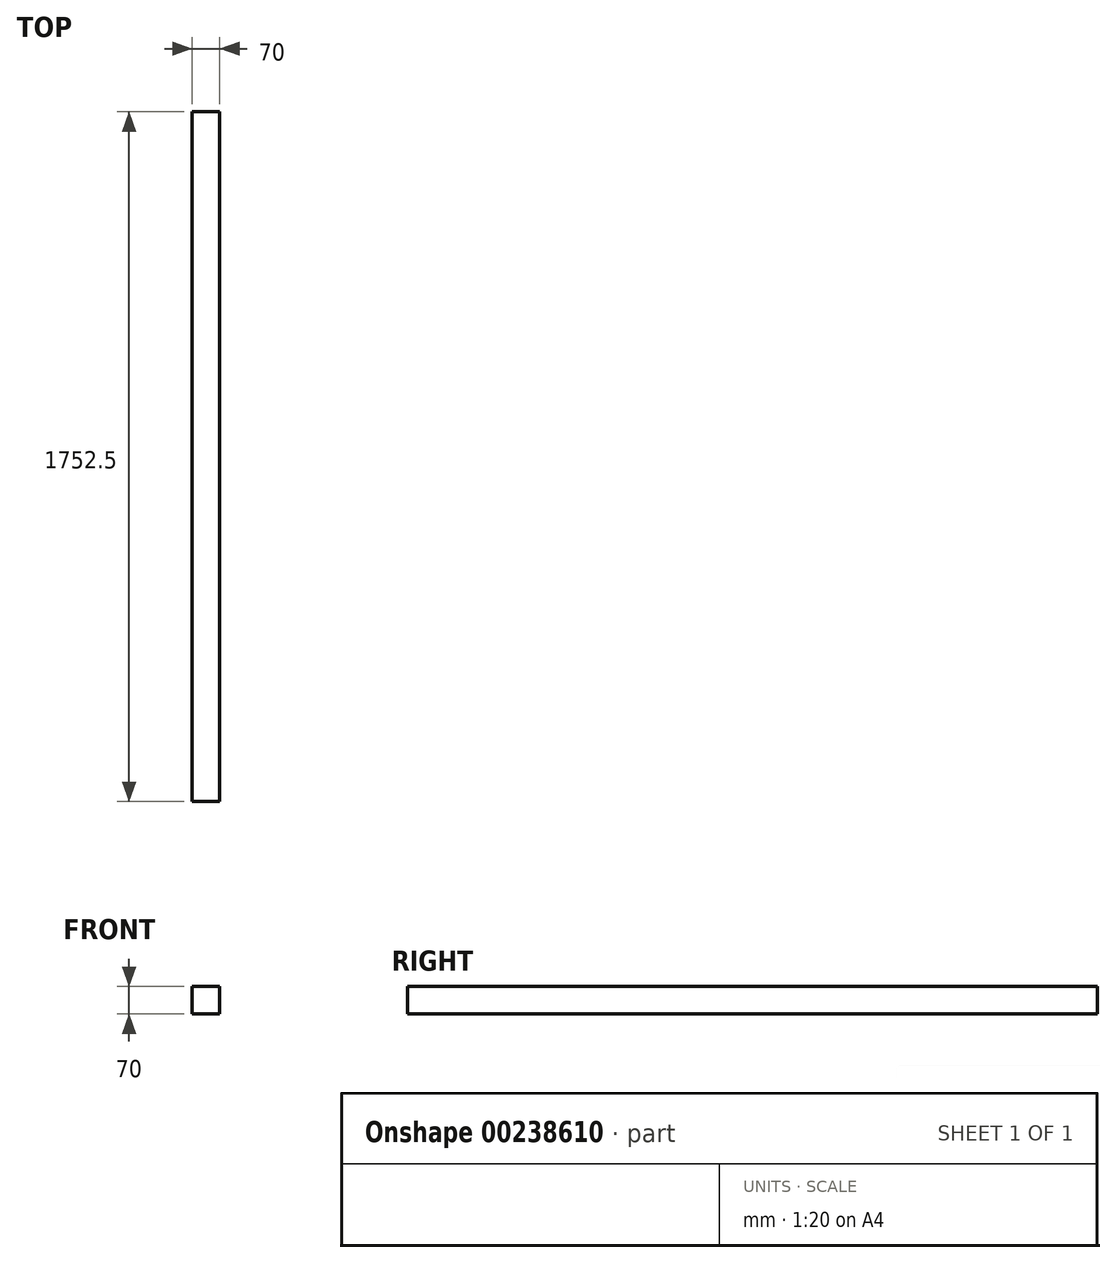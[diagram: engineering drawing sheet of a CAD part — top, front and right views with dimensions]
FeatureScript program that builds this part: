
annotation { "Feature Type Name" : "Feature", "Feature Type Description" : "" }
export const myFeature = defineFeature(function(context is Context, id is Id, definition is map)
    precondition{}
    {
        {
            var Q0;
            Q0=qCreatedBy(makeId("Front.planeOp"),FACE);
            var sketch = newSketch(context, id + "F0", { "sketchPlane" : qUnion([Q0])});
            skLineSegment(sketch, "E0.bottom", {"start": v(35, -35) * mm, "end": v(-35, -35) * mm});
            skLineSegment(sketch, "E0.top", {"start": v(35, 35) * mm, "end": v(-35, 35) * mm});
            skLineSegment(sketch, "E0.left", {"start": v(35, -35) * mm, "end": v(35, 35) * mm});
            skLineSegment(sketch, "E0.right", {"start": v(-35, -35) * mm, "end": v(-35, 35) * mm});
            skPoint(sketch, "E0.middle", {"position": v(0, 0) * mm});
            skSolve(sketch);
        }
        {
            var Q0;
            Q0=makeQuery(id+"F0.imprint","IMPRINT",FACE,{"disambiguationData":[TD([[makeQuery(id+"F0.imprint","IMPRINT",EDGE,{"derivedFrom":sQuery(id+"F0.wireOp",EDGE,"E0.bottom")}),-1.0]])]});
            extrude(context, id + "F1", {"entities" : qUnion([Q0]), "depth" : (1302.5 + 450) * mm});
        }
    });
